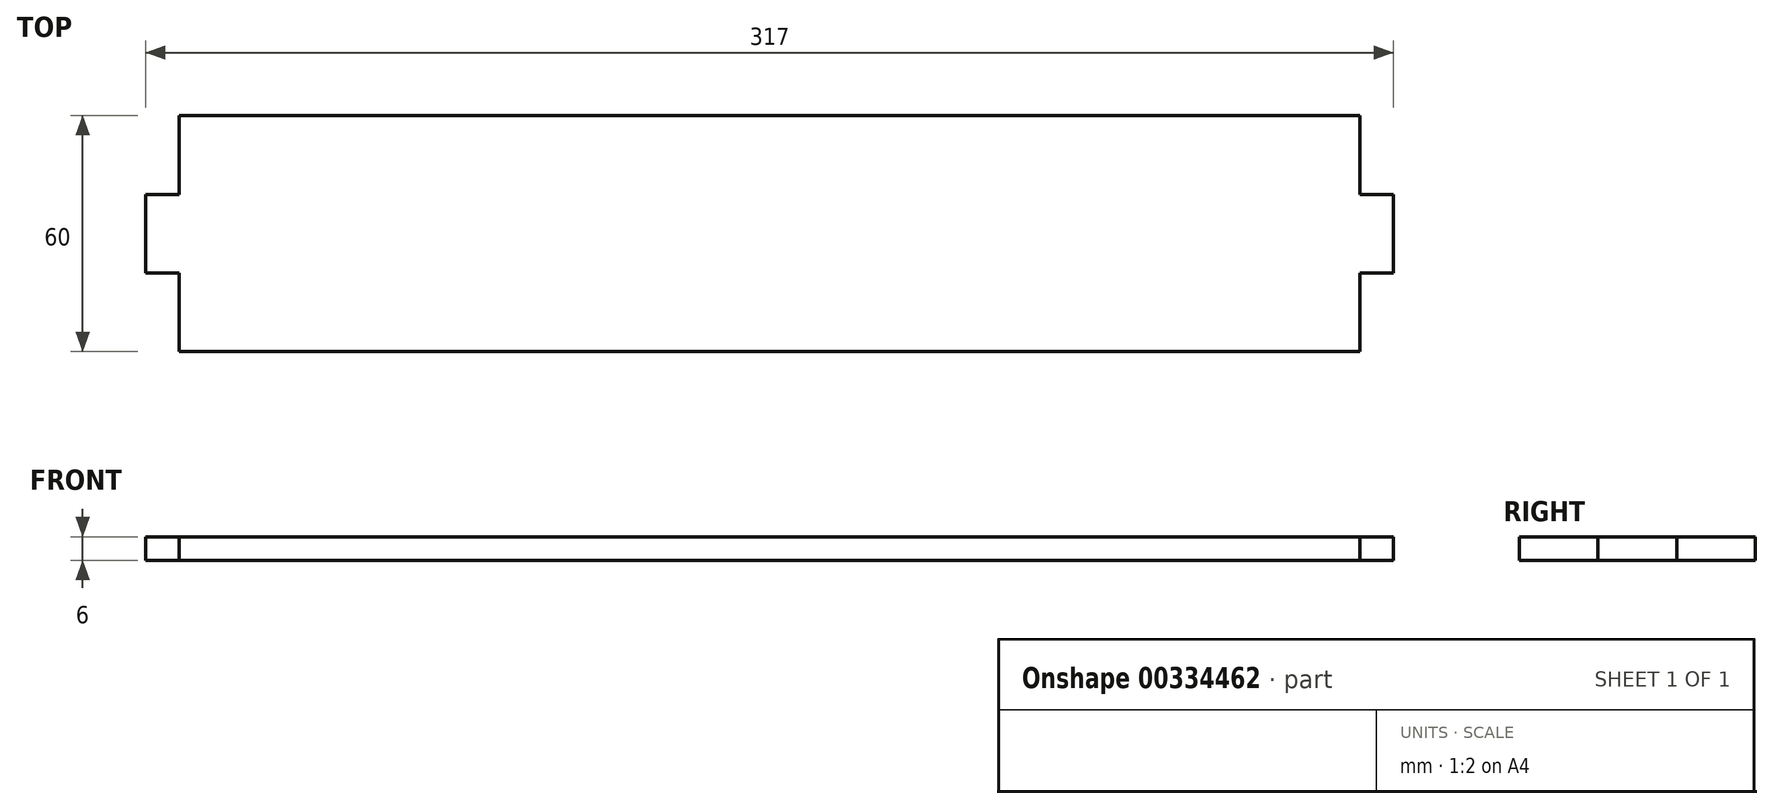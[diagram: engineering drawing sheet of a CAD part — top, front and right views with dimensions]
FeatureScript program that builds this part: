
annotation { "Feature Type Name" : "Feature", "Feature Type Description" : "" }
export const myFeature = defineFeature(function(context is Context, id is Id, definition is map)
    precondition{}
    {
        {
            var Q0;
            Q0=qCreatedBy(makeId("Top.planeOp"),FACE);
            var sketch = newSketch(context, id + "F0", { "sketchPlane" : qUnion([Q0])});
            skLineSegment(sketch, "E0.bottom", {"start": v(154.94, 30) * mm, "end": v(-145.06, 30) * mm});
            skLineSegment(sketch, "E0.top", {"start": v(154.94, -30) * mm, "end": v(-145.06, -30) * mm});
            skLineSegment(sketch, "E0.left", {"start": v(154.94, 30) * mm, "end": v(154.94, -30) * mm});
            skLineSegment(sketch, "E0.right", {"start": v(-145.06, 30) * mm, "end": v(-145.06, -30) * mm});
            skPoint(sketch, "E0.middle", {"position": v(4.94, 0) * mm});
            skSolve(sketch);
        }
        {
            var Q0;
            Q0 = qSketchRegion(id + "F0", true);
            extrude(context, id + "F1", {"entities" : qUnion([Q0]), "depth" : 6 * mm});
        }
        {
            var Q0;
            Q0=makeQuery(id+"F1.opExtrude","CAP_FACE",FACE,{"disambiguationData":[OSD([sQuery(id+"F0.wireOp",EDGE,"E0.bottom"),sQuery(id+"F0.wireOp",EDGE,"E0.top"),sQuery(id+"F0.wireOp",EDGE,"E0.left"),sQuery(id+"F0.wireOp",EDGE,"E0.right")])],"isStart":false});
            var sketch = newSketch(context, id + "F2", { "sketchPlane" : qUnion([Q0])});
            skLineSegment(sketch, "E1", {"start": v(-145.06, 0) * mm, "end": v(0, 0) * mm, "construction": true});
            skLineSegment(sketch, "E2", {"start": v(0, 0) * mm, "end": v(0, 30) * mm, "construction": true});
            skLineSegment(sketch, "E3", {"start": v(-145.06, 0) * mm, "end": v(-149.31, 0) * mm, "construction": true});
            skLineSegment(sketch, "E4.bottom", {"start": v(-145.06, 10) * mm, "end": v(-153.56, 10) * mm});
            skLineSegment(sketch, "E4.top", {"start": v(-145.06, -10) * mm, "end": v(-153.56, -10) * mm});
            skLineSegment(sketch, "E4.left", {"start": v(-145.06, 10) * mm, "end": v(-145.06, -10) * mm});
            skLineSegment(sketch, "E4.right", {"start": v(-153.56, 10) * mm, "end": v(-153.56, -10) * mm});
            skPoint(sketch, "E4.middle", {"position": v(-149.31, 0) * mm});
            skLineSegment(sketch, "E5", {"start": v(154.94, 0) * mm, "end": v(159.19, 0) * mm, "construction": true});
            skPoint(sketch, "E5.endSnap0", {"position": v(154.94, 0) * mm});
            skLineSegment(sketch, "E6.bottom", {"start": v(154.94, 10) * mm, "end": v(163.44, 10) * mm});
            skLineSegment(sketch, "E6.top", {"start": v(154.94, -10) * mm, "end": v(163.44, -10) * mm});
            skLineSegment(sketch, "E6.left", {"start": v(154.94, 10) * mm, "end": v(154.94, -10) * mm});
            skLineSegment(sketch, "E6.right", {"start": v(163.44, 10) * mm, "end": v(163.44, -10) * mm});
            skPoint(sketch, "E6.middle", {"position": v(159.19, 0) * mm});
            skSolve(sketch);
        }
        {
            var Q0;
            Q0 = qSketchRegion(id + "F2", true);
            var Q1;
            Q1=makeQuery(id+"F1.opExtrude","CAP_FACE",FACE,{"disambiguationData":[OSD([sQuery(id+"F0.wireOp",EDGE,"E0.bottom"),sQuery(id+"F0.wireOp",EDGE,"E0.top"),sQuery(id+"F0.wireOp",EDGE,"E0.left"),sQuery(id+"F0.wireOp",EDGE,"E0.right")])],"isStart":true});
            extrude(context, id + "F3", {"entities" : qUnion([Q0]), "operationType" : NewBodyOperationType.ADD, "endBound" : BoundingType.UP_TO_SURFACE, "oppositeDirection" : true, "endBoundEntityFace" : qUnion([Q1]), "depth" : 25 * mm});
        }
    });
